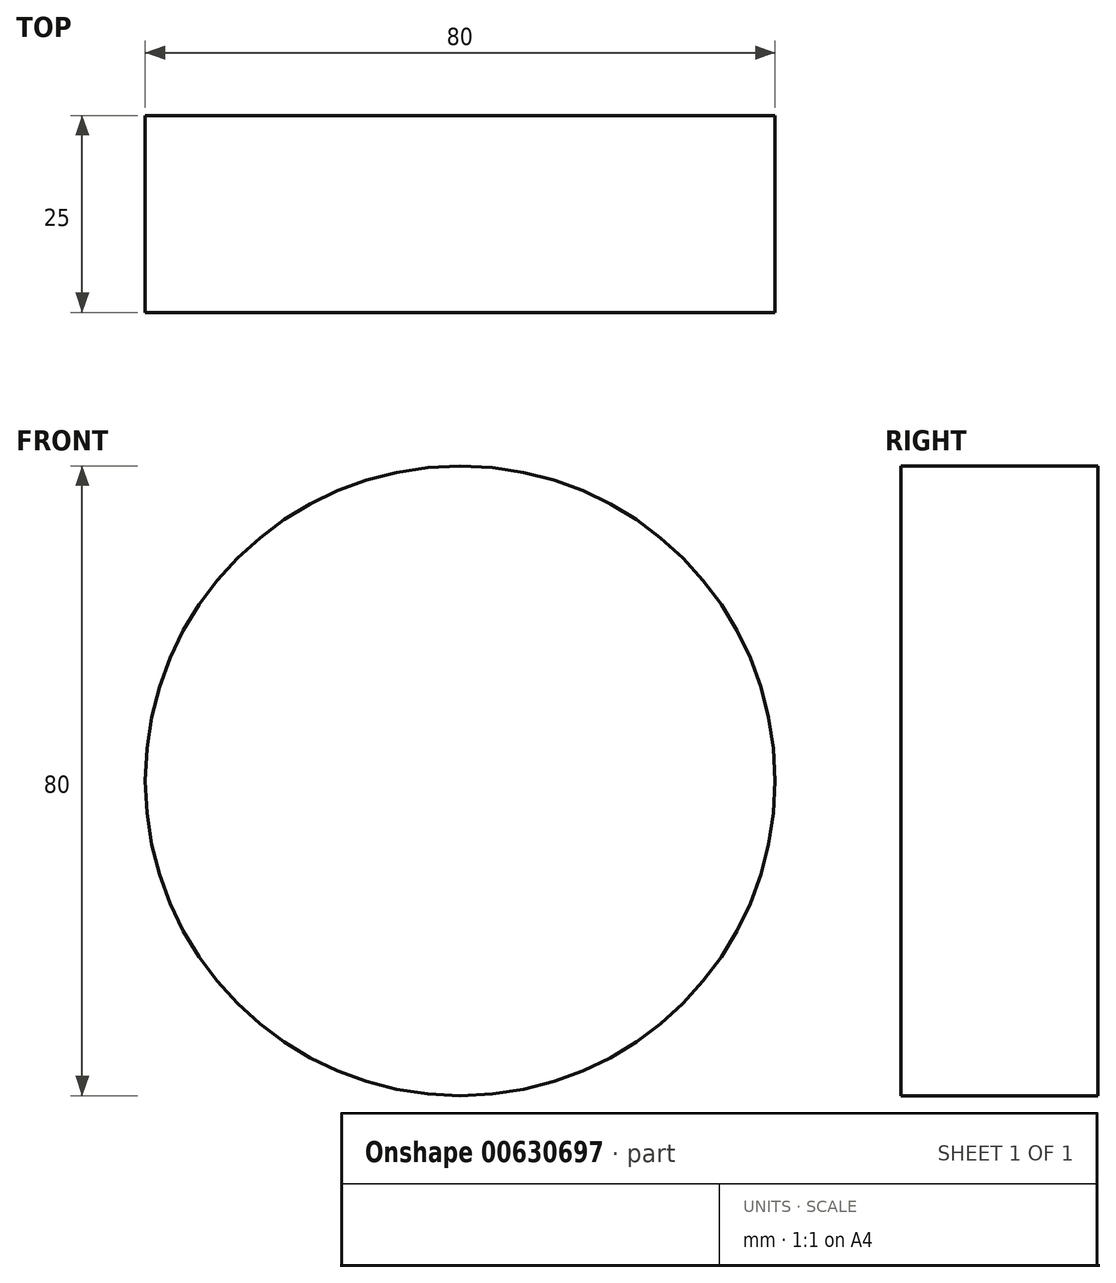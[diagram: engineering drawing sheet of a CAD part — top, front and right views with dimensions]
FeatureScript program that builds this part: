
annotation { "Feature Type Name" : "Feature", "Feature Type Description" : "" }
export const myFeature = defineFeature(function(context is Context, id is Id, definition is map)
    precondition{}
    {
        {
            var Q0;
            Q0=qCreatedBy(makeId("Front.planeOp"),FACE);
            var sketch = newSketch(context, id + "F0", { "sketchPlane" : qUnion([Q0])});
            skCircle(sketch, "E0", {"center": v(0, 0) * mm, "radius": 40 * mm});
            skSolve(sketch);
        }
        {
            var Q0;
            Q0=makeQuery(id+"F0.imprint","IMPRINT",FACE,{"disambiguationData":[TD([[makeQuery(id+"F0.imprint","IMPRINT",EDGE,{"derivedFrom":sQuery(id+"F0.wireOp",EDGE,"E0")}),1.0]])]});
            extrude(context, id + "F1", {"entities" : qUnion([Q0]), "depth" : 25 * mm, "offsetDistance" : 25 * mm});
        }
    });
